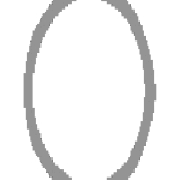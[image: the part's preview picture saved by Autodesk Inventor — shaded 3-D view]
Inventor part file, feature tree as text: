
AUTODESK INVENTOR PART (.ipt)
format: ipt  version: 2021 (Build 250183000, 183)  size: 116,224 bytes
history: native  units: in
note: dims shown in document units (in); Inventor stores cm internally (conversion verified against a paired STEP export)
features: other x4, sketch x3, plane x1
ambient origin geometry x8: Origin, YZ Plane, XZ Plane, XY Plane, X Axis, Y Axis, Z Axis, Center Point
bodies: Solid1 (feature_tree), Body (feature_tree)
feature tree (8):
  other  "Driven Length"
  other  "Frame Generator"
  other  "Start Plane"
  other  "End Plane"
  sketch  "Sketch"  dims[d2=3.0in d4=-0.0in d5=3.0in d6=0.12in d7=0.0in d8=90.0deg d9=3.0in]
  sketch  "Sketch2"  dims[d0=1.0in]
  plane  "Work Plane3"
  sketch  "Sketch3"  dims[d1=0.065in]
